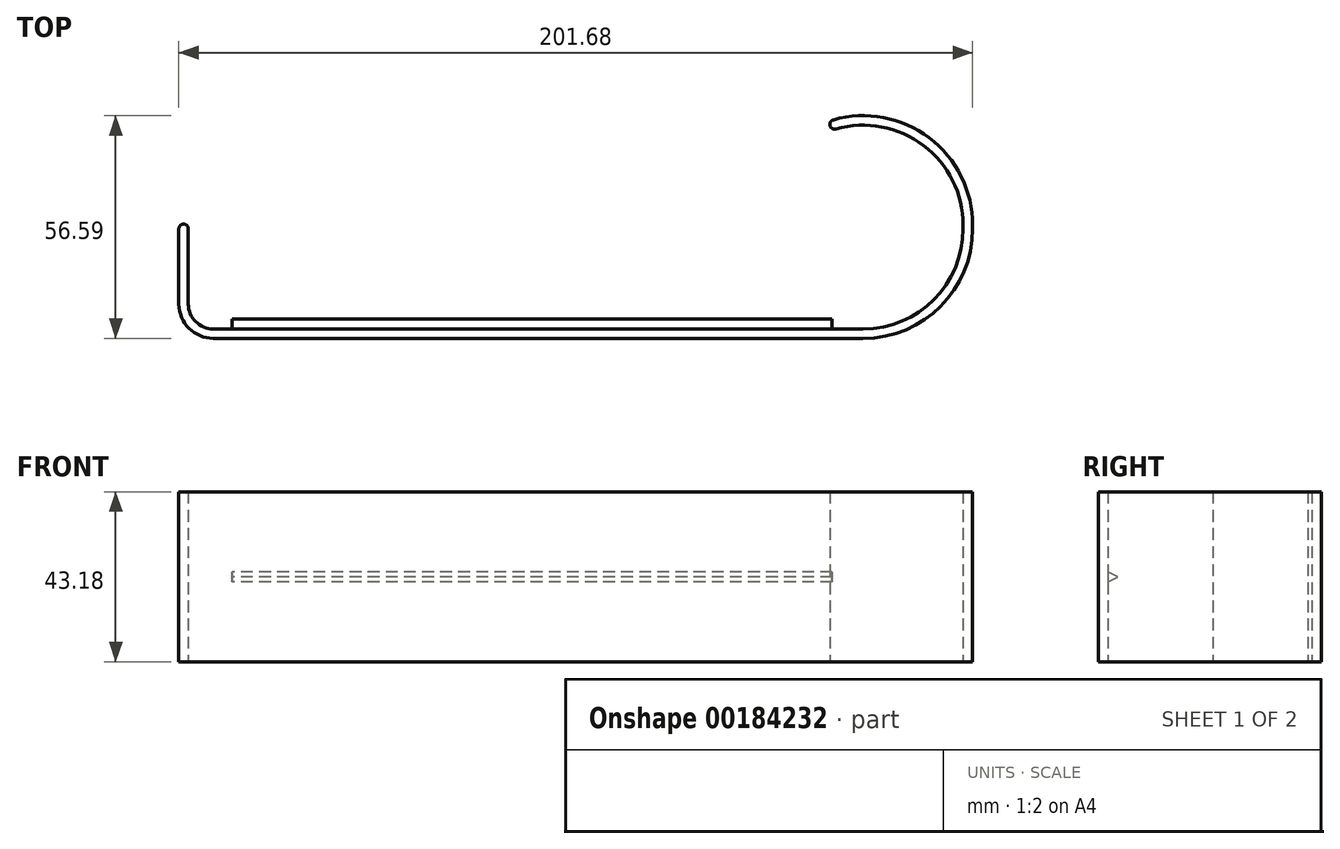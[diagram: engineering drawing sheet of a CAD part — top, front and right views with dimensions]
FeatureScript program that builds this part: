
annotation { "Feature Type Name" : "Feature", "Feature Type Description" : "" }
export const myFeature = defineFeature(function(context is Context, id is Id, definition is map)
    precondition{}
    {
        {
            var Q0;
            Q0=qCreatedBy(makeId("Top.planeOp"),FACE);
            var sketch = newSketch(context, id + "F0", { "sketchPlane" : qUnion([Q0])});
            skLineSegment(sketch, "E0", {"start": v(-55.62, 0) * mm, "end": v(109.48, 0) * mm});
            skLineSegment(sketch, "E1", {"start": v(134.88, 25.4) * mm, "end": v(134.88, 26.37) * mm});
            skLineSegment(sketch, "E2", {"start": v(-61.97, 6.35) * mm, "end": v(-61.97, 25.4) * mm});
            skPoint(sketch, "E3.visualSharp", {"position": v(-61.97, 0) * mm});
            skArc(sketch, "E3.filletArc", {"start": v(-61.97, 6.35) * mm, "mid": v(-60.11, 1.86) * mm, "end": v(-55.62, 0) * mm});
            skPoint(sketch, "E4.visualSharp", {"position": v(134.88, 0) * mm});
            skArc(sketch, "E4.filletArc", {"start": v(109.48, 0) * mm, "mid": v(127.44, 7.44) * mm, "end": v(134.88, 25.4) * mm});
            skPoint(sketch, "E5.visualSharp", {"position": v(134.88, 55.15) * mm});
            skArc(sketch, "E5.filletArc", {"start": v(134.88, 26.37) * mm, "mid": v(124.79, 46.64) * mm, "end": v(102.53, 50.8) * mm});
            skArc(sketch, "E6.0", {"start": v(137.29, 26.37) * mm, "mid": v(126.24, 48.56) * mm, "end": v(101.87, 53.12) * mm});
            skLineSegment(sketch, "E6.1", {"start": v(137.29, 25.4) * mm, "end": v(137.29, 26.37) * mm});
            skLineSegment(sketch, "E6.2", {"start": v(-64.39, 6.35) * mm, "end": v(-64.39, 25.4) * mm});
            skArc(sketch, "E6.3", {"start": v(-64.39, 6.35) * mm, "mid": v(-61.82, 0.15) * mm, "end": v(-55.62, -2.41) * mm});
            skLineSegment(sketch, "E6.4", {"start": v(-55.62, -2.41) * mm, "end": v(109.48, -2.41) * mm});
            skArc(sketch, "E6.5", {"start": v(109.48, -2.41) * mm, "mid": v(129.14, 5.73) * mm, "end": v(137.29, 25.4) * mm});
            skArc(sketch, "E7", {"start": v(101.87, 53.12) * mm, "mid": v(101.04, 51.63) * mm, "end": v(102.53, 50.8) * mm});
            skArc(sketch, "E8", {"start": v(-64.39, 25.4) * mm, "mid": v(-63.18, 26.6) * mm, "end": v(-61.97, 25.4) * mm});
            skSolve(sketch);
        }
        {
            var Q0;
            Q0=makeQuery(id+"F0.imprint","IMPRINT",FACE,{"disambiguationData":[TD([[makeQuery(id+"F0.imprint","IMPRINT",EDGE,{"derivedFrom":sQuery(id+"F0.wireOp",EDGE,"E0")}),-1.0]])]});
            extrude(context, id + "F1", {"entities" : qUnion([Q0]), "flatOperationType" : FlatOperationType.REMOVE, "offsetDistance" : 25.4 * mm, "depth" : 43.18 * mm, "domain" : OperationDomain.MODEL});
        }
        {
            var Q0;
            Q0=qCreatedBy(makeId("Right.planeOp"),FACE);
            var sketch = newSketch(context, id + "F2", { "sketchPlane" : qUnion([Q0])});
            skLineSegment(sketch, "E9", {"start": v(0, 22.86) * mm, "end": v(0, 20.32) * mm});
            skLineSegment(sketch, "E10", {"start": v(0, 20.32) * mm, "end": v(2.54, 21.6) * mm});
            skLineSegment(sketch, "E11", {"start": v(2.54, 21.59) * mm, "end": v(0, 22.86) * mm});
            skSolve(sketch);
        }
        {
            var Q0;
            Q0=makeQuery(id+"F2.imprint","IMPRINT",FACE,{"disambiguationData":[TD([[makeQuery(id+"F2.imprint","IMPRINT",EDGE,{"derivedFrom":sQuery(id+"F2.wireOp",EDGE,"E9")}),1.0]])]});
            extrude(context, id + "F3", {"entities" : qUnion([Q0]), "operationType" : NewBodyOperationType.ADD, "depth" : 101.6 * mm, "hasSecondDirection" : true, "secondDirectionOppositeDirection" : true, "secondDirectionDepth" : 50.8 * mm});
        }
    });
